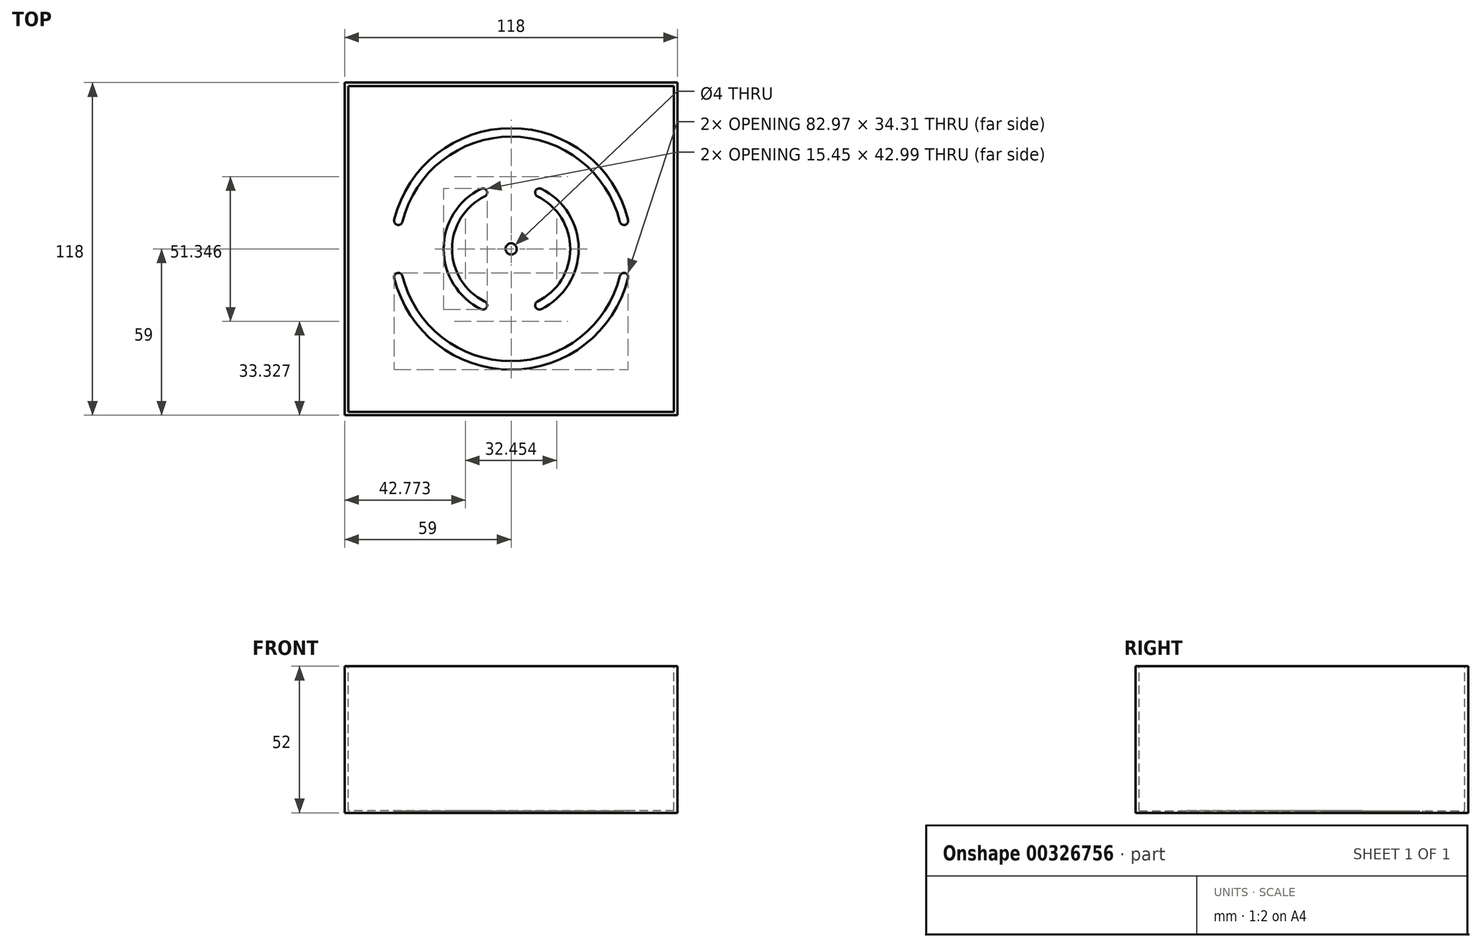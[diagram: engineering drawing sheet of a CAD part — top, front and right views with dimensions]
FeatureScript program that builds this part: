
annotation { "Feature Type Name" : "Feature", "Feature Type Description" : "" }
export const myFeature = defineFeature(function(context is Context, id is Id, definition is map)
    precondition{}
    {
        {
            var Q0;
            Q0=qCreatedBy(makeId("Top.planeOp"),FACE);
            var sketch = newSketch(context, id + "F0", { "sketchPlane" : qUnion([Q0])});
            skLineSegment(sketch, "E0.bottom", {"start": v(59, -59) * mm, "end": v(-59, -59) * mm});
            skLineSegment(sketch, "E0.top", {"start": v(59, 59) * mm, "end": v(-59, 59) * mm});
            skLineSegment(sketch, "E0.left", {"start": v(59, -59) * mm, "end": v(59, 59) * mm});
            skLineSegment(sketch, "E0.right", {"start": v(-59, -59) * mm, "end": v(-59, 59) * mm});
            skPoint(sketch, "E0.middle", {"position": v(0, 0) * mm});
            skSolve(sketch);
        }
        {
            var Q0;
            Q0 = qSketchRegion(id + "F0", true);
            extrude(context, id + "F1", {"entities" : qUnion([Q0]), "depth" : 52 * mm});
        }
        {
            var Q0;
            Q0=makeQuery(id+"F1.opExtrude","CAP_FACE",FACE,{"disambiguationData":[OSD([sQuery(id+"F0.wireOp",EDGE,"E0.bottom"),sQuery(id+"F0.wireOp",EDGE,"E0.top"),sQuery(id+"F0.wireOp",EDGE,"E0.left"),sQuery(id+"F0.wireOp",EDGE,"E0.right")])],"isStart":false});
            var sketch = newSketch(context, id + "F2", { "sketchPlane" : qUnion([Q0])});
            skLineSegment(sketch, "E1.bottom", {"start": v(57.75, -57.75) * mm, "end": v(-57.75, -57.75) * mm});
            skLineSegment(sketch, "E1.top", {"start": v(57.75, 57.75) * mm, "end": v(-57.75, 57.75) * mm});
            skLineSegment(sketch, "E1.left", {"start": v(57.75, -57.75) * mm, "end": v(57.75, 57.75) * mm});
            skLineSegment(sketch, "E1.right", {"start": v(-57.75, -57.75) * mm, "end": v(-57.75, 57.75) * mm});
            skPoint(sketch, "E1.middle", {"position": v(0, 0) * mm});
            skSolve(sketch);
        }
        {
            var Q0;
            Q0 = qSketchRegion(id + "F2", true);
            extrude(context, id + "F3", {"entities" : qUnion([Q0]), "operationType" : NewBodyOperationType.REMOVE, "oppositeDirection" : true, "depth" : 51.3 * mm});
        }
        {
            var Q0;
            Q0=makeQuery(id+"F1.opExtrude","CAP_FACE",FACE,{"disambiguationData":[OSD([sQuery(id+"F0.wireOp",EDGE,"E0.bottom"),sQuery(id+"F0.wireOp",EDGE,"E0.top"),sQuery(id+"F0.wireOp",EDGE,"E0.left"),sQuery(id+"F0.wireOp",EDGE,"E0.right")])],"isStart":true});
            var sketch = newSketch(context, id + "F4", { "sketchPlane" : qUnion([Q0])});
            skLineSegment(sketch, "E2", {"start": v(-40, 10) * mm, "end": v(40, 10) * mm, "construction": true});
            skArc(sketch, "E3", {"start": v(40, 10) * mm, "mid": v(0, 41.33) * mm, "end": v(-40, 10) * mm, "construction": true});
            skArc(sketch, "E4.0.startCap", {"start": v(41.46, 10.36) * mm, "mid": v(40.36, 8.54) * mm, "end": v(38.54, 9.64) * mm});
            skArc(sketch, "E4.0.endCap", {"start": v(-38.54, 9.64) * mm, "mid": v(-40.36, 8.54) * mm, "end": v(-41.46, 10.36) * mm});
            skArc(sketch, "E4.0.left", {"start": v(38.54, 9.64) * mm, "mid": v(0, 39.83) * mm, "end": v(-38.54, 9.64) * mm});
            skArc(sketch, "E4.0.right", {"start": v(41.46, 10.36) * mm, "mid": v(0, 42.83) * mm, "end": v(-41.46, 10.36) * mm});
            skArc(sketch, "E5.MirrorCS", {"start": v(38.54, -9.64) * mm, "mid": v(0, -39.83) * mm, "end": v(-38.54, -9.64) * mm});
            skArc(sketch, "E6.MirrorCS", {"start": v(-38.54, -9.64) * mm, "mid": v(-40.36, -8.54) * mm, "end": v(-41.46, -10.36) * mm});
            skArc(sketch, "E7.MirrorCS", {"start": v(41.46, -10.36) * mm, "mid": v(0, -42.83) * mm, "end": v(-41.46, -10.36) * mm});
            skArc(sketch, "E8.MirrorCS", {"start": v(41.46, -10.36) * mm, "mid": v(40.36, -8.54) * mm, "end": v(38.54, -9.64) * mm});
            skLineSegment(sketch, "E9", {"start": v(10, -20) * mm, "end": v(10, 20) * mm, "construction": true});
            skArc(sketch, "E10", {"start": v(10, -20) * mm, "mid": v(22.45, 0) * mm, "end": v(10, 20) * mm, "construction": true});
            skArc(sketch, "E11.0.startCap", {"start": v(10.66, -21.35) * mm, "mid": v(8.65, -20.66) * mm, "end": v(9.34, -18.65) * mm});
            skArc(sketch, "E11.0.endCap", {"start": v(9.34, 18.65) * mm, "mid": v(8.65, 20.66) * mm, "end": v(10.66, 21.35) * mm});
            skArc(sketch, "E11.0.left", {"start": v(9.34, -18.65) * mm, "mid": v(20.95, 0) * mm, "end": v(9.34, 18.65) * mm});
            skArc(sketch, "E11.0.right", {"start": v(10.66, -21.35) * mm, "mid": v(23.95, 0) * mm, "end": v(10.66, 21.35) * mm});
            skArc(sketch, "E12.MirrorCS", {"start": v(-10, -20) * mm, "mid": v(-22.45, 0) * mm, "end": v(-10, 20) * mm, "construction": true});
            skArc(sketch, "E13.MirrorCS", {"start": v(-9.34, 18.65) * mm, "mid": v(-8.65, 20.66) * mm, "end": v(-10.66, 21.35) * mm});
            skArc(sketch, "E14.MirrorCS", {"start": v(-10.66, -21.35) * mm, "mid": v(-23.95, 0) * mm, "end": v(-10.66, 21.35) * mm});
            skArc(sketch, "E15.MirrorCS", {"start": v(-9.34, -18.65) * mm, "mid": v(-20.95, 0) * mm, "end": v(-9.34, 18.65) * mm});
            skArc(sketch, "E16.MirrorCS", {"start": v(-10.66, -21.35) * mm, "mid": v(-8.65, -20.66) * mm, "end": v(-9.34, -18.65) * mm});
            skCircle(sketch, "E17", {"center": v(0, 0) * mm, "radius": 2 * mm});
            skSolve(sketch);
        }
        {
            var Q0;
            Q0 = qSketchRegion(id + "F4", true);
            extrude(context, id + "F5", {"entities" : qUnion([Q0]), "operationType" : NewBodyOperationType.REMOVE, "oppositeDirection" : true, "depth" : 25 * mm});
        }
    });
